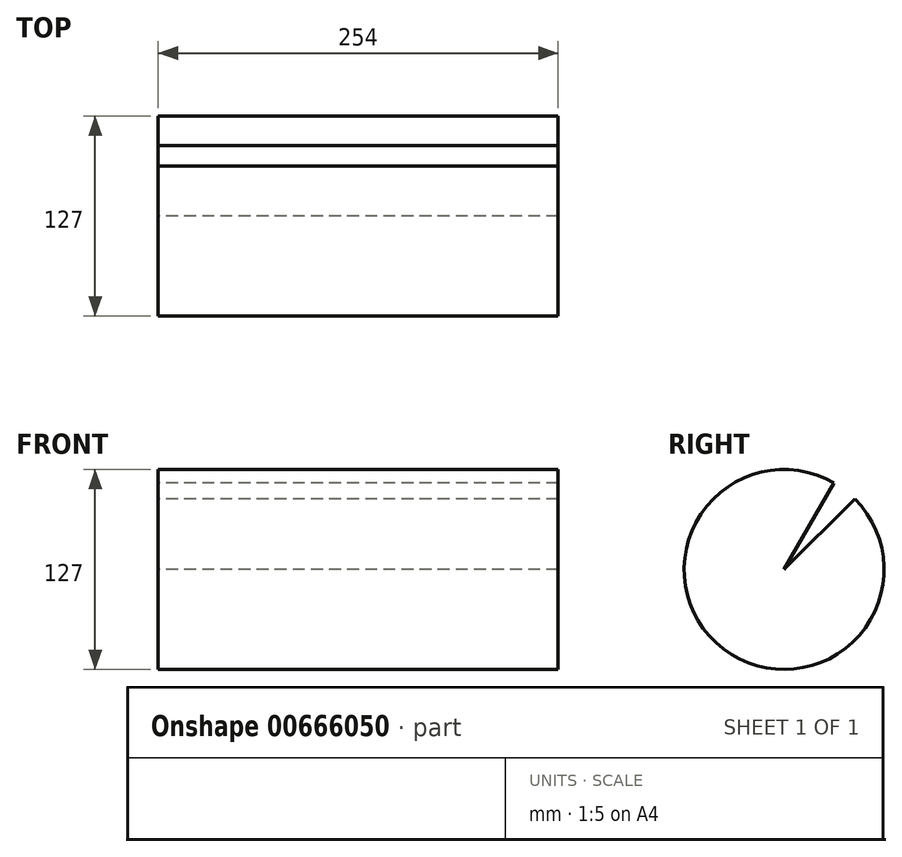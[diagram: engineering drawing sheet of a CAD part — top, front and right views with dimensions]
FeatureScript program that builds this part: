
annotation { "Feature Type Name" : "Feature", "Feature Type Description" : "" }
export const myFeature = defineFeature(function(context is Context, id is Id, definition is map)
    precondition{}
    {
        {
            var Q0;
            Q0=qCreatedBy(makeId("Right.planeOp"),FACE);
            var sketch = newSketch(context, id + "F0", { "sketchPlane" : qUnion([Q0])});
            skLineSegment(sketch, "E0", {"start": v(0, 67.06) * mm, "end": v(0, -73.8) * mm, "construction": true});
            skArc(sketch, "E1", {"start": v(31.75, 55) * mm, "mid": v(-38.66, -50.38) * mm, "end": v(44.9, 44.9) * mm});
            skLineSegment(sketch, "E2", {"start": v(31.75, 55) * mm, "end": v(0, 0) * mm});
            skLineSegment(sketch, "E3", {"start": v(44.9, 44.9) * mm, "end": v(0, 0) * mm});
            skSolve(sketch);
        }
        {
            var Q0;
            Q0=makeQuery(id+"F0.imprint","IMPRINT",FACE,{"disambiguationData":[TD([[makeQuery(id+"F0.imprint","IMPRINT",EDGE,{"derivedFrom":sQuery(id+"F0.wireOp",EDGE,"E1")}),1.0]])]});
            extrude(context, id + "F1", {"entities" : qUnion([Q0]), "depth" : 127 * mm, "offsetDistance" : 25.4 * mm, "hasSecondDirection" : true, "secondDirectionOppositeDirection" : true, "secondDirectionDepth" : 127 * mm});
        }
    });
